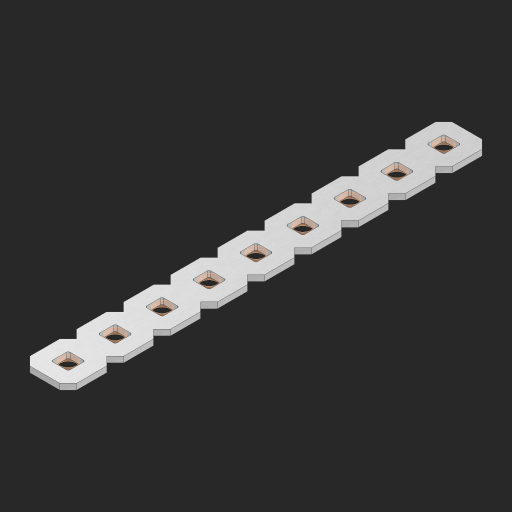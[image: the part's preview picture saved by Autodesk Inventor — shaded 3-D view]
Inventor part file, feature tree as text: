
AUTODESK INVENTOR PART (.ipt)
format: ipt  version: 2023 (Build 270158000, 158)  size: 362,496 bytes
history: native  units: in
note: dims shown in document units (in); Inventor stores cm internally (conversion verified against a paired STEP export)
features: other x10, extrude x8, sketch x2, pattern_linear x1
ambient origin geometry x8: Origin, YZ Plane, XZ Plane, XY Plane, X Axis, Y Axis, Z Axis, Center Point
bodies: Solid1 (feature_tree), Body (feature_tree)
feature tree (21):
  pattern_linear  "Rectangular Pattern1"  Spacing1=0.09in  [1 undecoded]
  sketch  "Sketch1"  dims[d1=0.5in]
  sketch  "Sketch2"  dims[d2=0.182in d3=0.09in d4=0.09in d5=0.09in d6=0.09in d7=0.09in d8=0.09in d9=0.09in d10=0.09in d11=0.02in d13=0.0in d14=0.172in d15=0.0625in d16=0.0in d19=0.5in d22=0.5in]
  other  "Srf1"
  other  "Srf126"
  other  "Srf127"
  other  "Srf128"
  other  "Srf129"
  other  "Srf130"
  other  "Srf131"
  other  "Srf250"
  other  "Srf251"
  other  "Circle"
  extrude  "ExtrusionSrf126"  Depth=0.09in
  extrude  "ExtrusionSrf127"  Depth=0.09in
  extrude  "ExtrusionSrf128"  Depth=0.09in
  extrude  "ExtrusionSrf129"  Depth=0.09in
  extrude  "ExtrusionSrf130"  Depth=0.09in
  extrude  "ExtrusionSrf131"  Depth=0.09in
  extrude  "ExtrusionSrf250"  Depth=0.09in
  extrude  "ExtrusionSrf251"  Depth=0.02in
note: 1 required parameter value undecoded (feature->parameter linkage not recoverable at this tier; creation-order binding heuristic only, values carry confidence <= 0.55)
